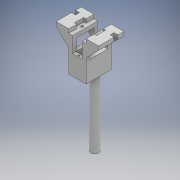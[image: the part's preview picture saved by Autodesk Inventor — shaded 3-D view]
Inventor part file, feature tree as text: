
AUTODESK INVENTOR PART (.ipt)
format: ipt  version: 2018 (Build 220112000, 112)  size: 327,680 bytes
history: native  units: mm
features: extrude x14, sketch x14, other x3, fillet x1, chamfer x1
ambient origin geometry x8: Origin, YZ Plane, XZ Plane, XY Plane, X Axis, Y Axis, Z Axis, Center Point
bodies: Solid1 (feature_tree)
feature tree (33):
  extrude  "base"  Depth=32.0mm
  extrude  "servo_place"  Depth=25.0mm
  extrude  "attacher"  Depth=23.0mm
  fillet  "Fillet2"  Radius=23.0mm
  extrude  "screws_servo"  Depth=18.0mm TaperAngle=0.0deg
  extrude  "hole_bar_rigify"  Depth=2.0mm
  extrude  "pilars_top"  Depth=2.0mm
  extrude  "base_top"  Depth=10.0mm
  chamfer  "Chamfer1"  Distance=120.0mm
  extrude  "screw_hole"  Depth=5.0mm
  extrude  "Extrusion11"  Depth=20.0mm TaperAngle=0.0deg
  extrude  "Extrusión12"  Depth=18.0mm
  extrude  "Extrusión13"  Depth=18.0mm TaperAngle=45.0deg
  other  "Edición directa1"
  extrude  "Extrusión14"  Depth=5.0mm TaperAngle=0.0deg
  extrude  "Extrusión15"  Depth=5.0mm
  extrude  "Extrusión16"  Depth=5.0mm
  sketch  "Sketch1"  dims[d0=18.0mm d1=32.0mm]
  sketch  "Sketch2"  dims[d2=25.0mm d3=0.0mm d4=11.5mm]
  sketch  "Sketch3"  dims[d5=90.0deg d6=6.25mm d7=23.0mm]
  sketch  "Sketch4"  dims[d8=12.5mm d9=18.0mm d10=0.0mm]
  sketch  "Sketch5"  dims[d11=2.8mm d12=2.0mm]
  sketch  "Sketch6"  dims[d13=2.8mm d14=2.0mm]
  sketch  "Sketch9"  dims[d15=17.0mm d16=0.0mm d18=10.0mm]
  sketch  "Sketch10"  dims[d19=10.0mm d20=120.0mm d21=0.0mm]
  sketch  "Sketch11"  dims[d22=4.0mm d23=5.0mm]
  sketch  "Boceto12"  dims[d24=12.0mm d25=0.0mm d26=20.0mm d27=0.0mm]
  sketch  "Boceto13"  dims[d39=18.0mm d40=18.0mm]
  sketch  "Boceto14"  dims[d41=5.0mm d42=0.0mm d43=18.0mm d44=2.0mm d45=45.0deg]
  sketch  "Boceto15"  dims[d46=12.0mm d47=5.0mm d48=0.0mm]
  sketch  "Boceto16"  dims[d49=2.5mm d50=5.0mm d51=5.0mm d52=2.5mm d53=5.0mm d54=5.0mm d55=5.0mm d56=0.0mm d57=30.0mm d58=0.0mm d59=13.0mm d60=90.0deg d61=3.5mm d62=3.5mm d63=0.5mm d64=6.0mm d65=8.0mm d66=5.0mm d67=0.0mm d68=0.0mm d69=0.0mm d70=2.0mm d71=0.0mm d72=0.0mm d73=2.0mm d74=4.75mm d75=10.0mm d76=3.0mm d77=10.0mm d78=10.0mm d79=3.0mm d80=5.0mm d81=0.0mm d82=5.0mm d83=5.0mm d84=5.0mm d85=0.0mm d86=4.0mm d87=3.0mm d88=4.0mm d89=3.0mm d90=5.0mm d91=0.0mm]
  other  "Desplazar1"
  other  "Desplazar2"
